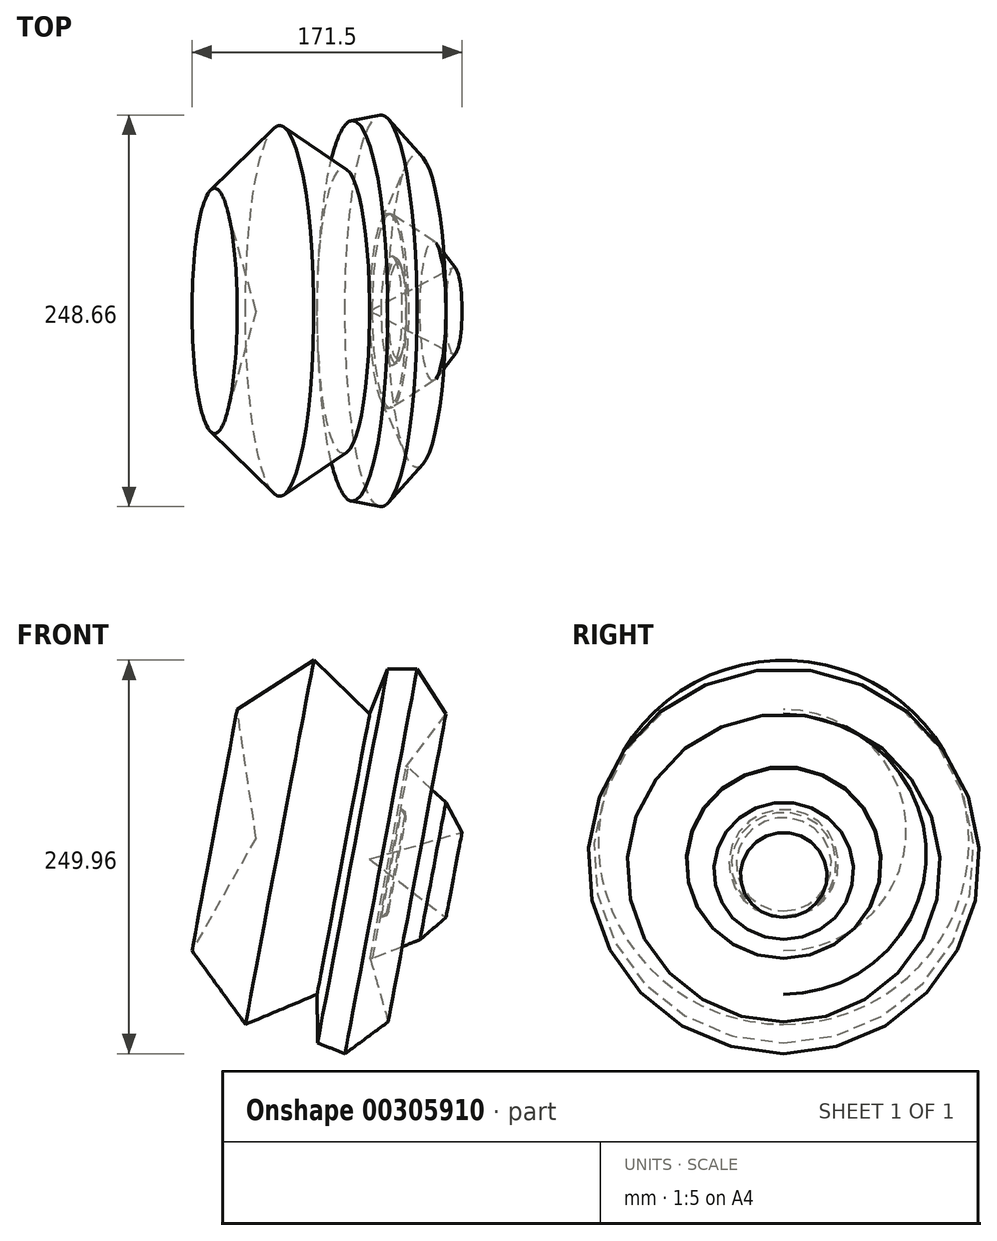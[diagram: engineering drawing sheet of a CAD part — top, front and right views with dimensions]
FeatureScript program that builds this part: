
annotation { "Feature Type Name" : "Feature", "Feature Type Description" : "" }
export const myFeature = defineFeature(function(context is Context, id is Id, definition is map)
    precondition{}
    {
        {
            var Q0;
            Q0=qCreatedBy(makeId("Front.planeOp"),FACE);
            var sketch = newSketch(context, id + "F0", { "sketchPlane" : qUnion([Q0])});
            skLineSegment(sketch, "E0", {"start": v(-29.9, -51.89) * mm, "end": v(32.84, -39.57) * mm});
            skLineSegment(sketch, "E1", {"start": v(32.54, -36.35) * mm, "end": v(-9.68, -2.92) * mm});
            skLineSegment(sketch, "E2", {"start": v(-9.68, -2.92) * mm, "end": v(-69.2, 19.94) * mm});
            skLineSegment(sketch, "E3", {"start": v(-69.2, 19.94) * mm, "end": v(-18.76, 34.6) * mm});
            skLineSegment(sketch, "E4", {"start": v(-18.76, 34.6) * mm, "end": v(-34.3, 16.43) * mm});
            skLineSegment(sketch, "E5", {"start": v(-34.3, 16.43) * mm, "end": v(-4.4, 9.1) * mm});
            skLineSegment(sketch, "E6", {"start": v(2.05, 17.9) * mm, "end": v(9.68, 26.1) * mm});
            skLineSegment(sketch, "E7", {"start": v(2.05, 17.9) * mm, "end": v(32.84, -39.57) * mm});
            skLineSegment(sketch, "E8", {"start": v(2.05, 17.9) * mm, "end": v(-4.4, 9.1) * mm});
            skLineSegment(sketch, "E9", {"start": v(32.84, -39.57) * mm, "end": v(32.54, -36.35) * mm});
            skLineSegment(sketch, "E10", {"start": v(9.68, 26.1) * mm, "end": v(21.1, 54.83) * mm});
            skLineSegment(sketch, "E11", {"start": v(21.1, 54.83) * mm, "end": v(39.87, 54.83) * mm});
            skLineSegment(sketch, "E12", {"start": v(39.87, 54.83) * mm, "end": v(58.05, 26.1) * mm});
            skLineSegment(sketch, "E13", {"start": v(58.05, 26.1) * mm, "end": v(32.84, -7.32) * mm});
            skLineSegment(sketch, "E14", {"start": v(34.3, -7.9) * mm, "end": v(58.05, -29.96) * mm});
            skLineSegment(sketch, "E15", {"start": v(34.3, -7.9) * mm, "end": v(32.84, -7.32) * mm});
            skLineSegment(sketch, "E16", {"start": v(58.05, -29.96) * mm, "end": v(68.31, -48.95) * mm});
            skLineSegment(sketch, "E17", {"start": v(68.31, -48.95) * mm, "end": v(9.68, -66) * mm});
            skLineSegment(sketch, "E18", {"start": v(9.68, -66) * mm, "end": v(-62.45, -52.47) * mm});
            skLineSegment(sketch, "E19", {"start": v(-62.45, -52.47) * mm, "end": v(-74.47, 29.03) * mm});
            skLineSegment(sketch, "E20", {"start": v(-74.47, 29.03) * mm, "end": v(-25.8, 60.4) * mm});
            skLineSegment(sketch, "E21", {"start": v(-25.8, 60.4) * mm, "end": v(9.68, 26.1) * mm});
            skLineSegment(sketch, "E22", {"start": v(-29.9, -51.89) * mm, "end": v(-9.68, -2.92) * mm});
            skSolve(sketch);
        }
        {
            var Q0;
            {var subQ0=sQuery(id+"F0.wireOp",EDGE,"E0");Q0=makeQuery(id+"F0.imprint","IMPRINT",FACE,{"disambiguationData":[TD([[makeQuery(id+"F0.imprint","IMPRINT",EDGE,{"derivedFrom":subQ0}),1.0]])]});}
            var Q1;
            {var subQ0=sQuery(id+"F0.wireOp",EDGE,"E2");Q1=makeQuery(id+"F0.imprint","IMPRINT",FACE,{"disambiguationData":[TD([[makeQuery(id+"F0.imprint","IMPRINT",EDGE,{"derivedFrom":subQ0}),-1.0]])]});}
            var Q2;
            Q2=makeQuery(id+"F0.imprint","IMPRINT",FACE,{"disambiguationData":[TD([[makeQuery(id+"F0.imprint","IMPRINT",EDGE,{"derivedFrom":sQuery(id+"F0.wireOp",EDGE,"E0")}),-1.0]])]});
            var Q3;
            Q3=sQuery(id+"F0.wireOp",EDGE,"E18");
            revolve(context, id + "F1", {"entities" : qUnion([Q0, Q1, Q2]), "axis" : qUnion([Q3]), "revolveType" : RevolveType.FULL});
        }
    });
